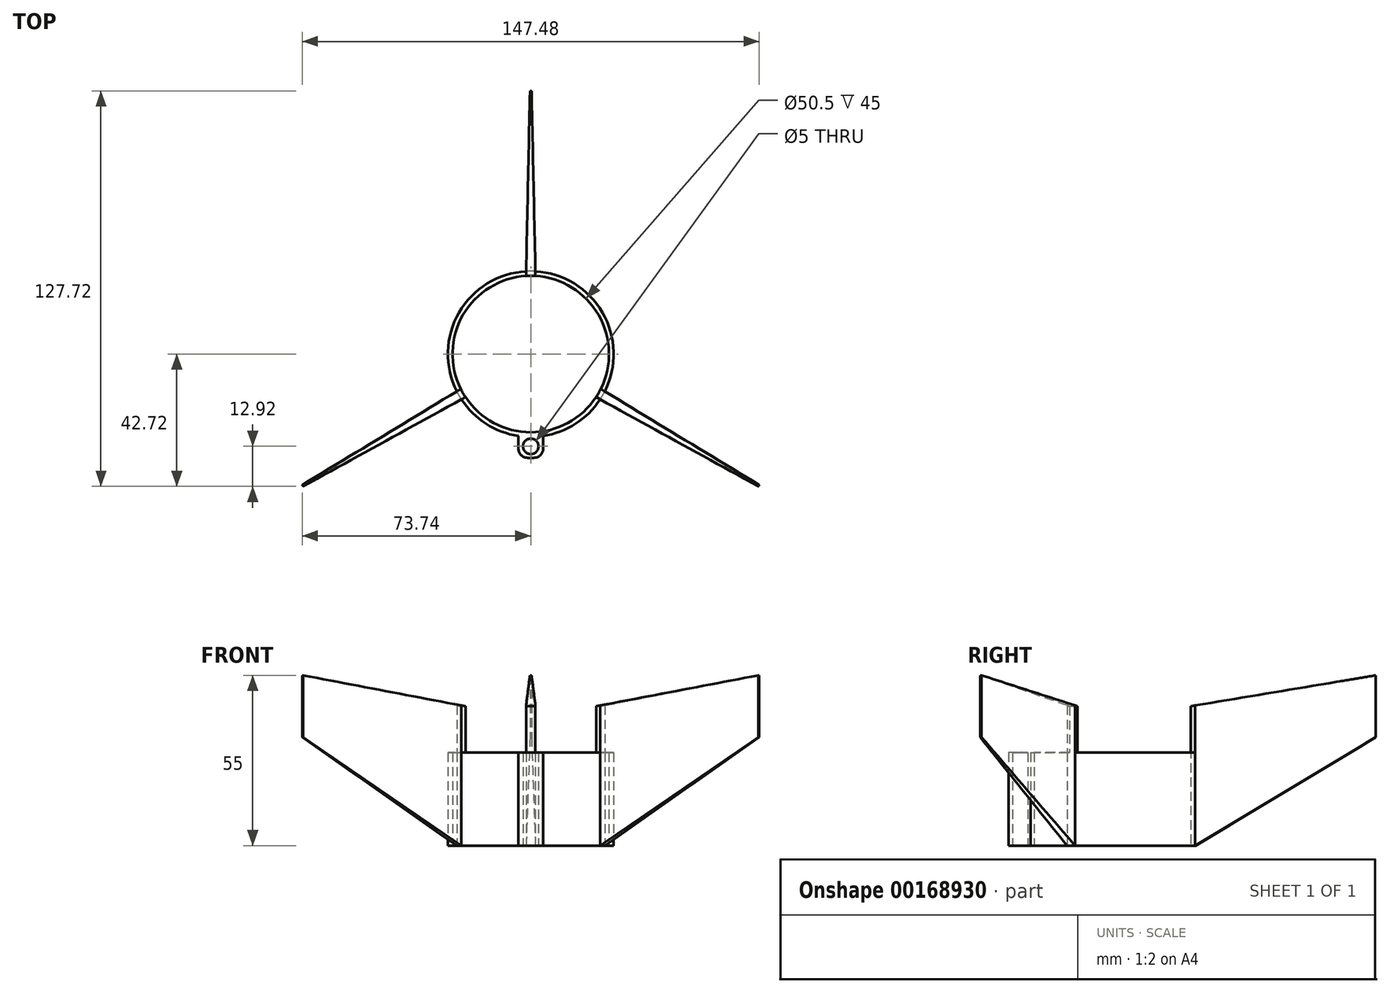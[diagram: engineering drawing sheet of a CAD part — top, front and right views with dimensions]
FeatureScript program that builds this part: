
annotation { "Feature Type Name" : "Feature", "Feature Type Description" : "" }
export const myFeature = defineFeature(function(context is Context, id is Id, definition is map)
    precondition{}
    {
        {
            var Q0;
            Q0=qCreatedBy(makeId("Top.planeOp"),FACE);
            var sketch = newSketch(context, id + "F0", { "sketchPlane" : qUnion([Q0])});
            skCircle(sketch, "E0", {"center": v(0, 0) * mm, "radius": 25.25 * mm});
            skArc(sketch, "E1", {"start": v(-22.38, -14.65) * mm, "mid": v(0, -26.75) * mm, "end": v(22.38, -14.65) * mm});
            skLineSegment(sketch, "E2", {"start": v(0, 0) * mm, "end": v(0, 85) * mm, "construction": true});
            skLineSegment(sketch, "E3", {"start": v(0, 0) * mm, "end": v(73.61, -42.5) * mm, "construction": true});
            skLineSegment(sketch, "E4", {"start": v(0, 0) * mm, "end": v(-73.61, -42.5) * mm, "construction": true});
            skLineSegment(sketch, "E5", {"start": v(0, 85) * mm, "end": v(1.5, 85) * mm});
            skLineSegment(sketch, "E6", {"start": v(0, 85) * mm, "end": v(-1.5, 85) * mm});
            skLineSegment(sketch, "E7", {"start": v(73.61, -42.5) * mm, "end": v(74.36, -41.2) * mm});
            skLineSegment(sketch, "E8", {"start": v(73.61, -42.5) * mm, "end": v(72.86, -43.8) * mm});
            skLineSegment(sketch, "E9", {"start": v(-73.61, -42.5) * mm, "end": v(-74.36, -41.2) * mm});
            skLineSegment(sketch, "E10", {"start": v(-73.61, -42.5) * mm, "end": v(-72.86, -43.8) * mm});
            skLineSegment(sketch, "E11", {"start": v(-1.5, 85) * mm, "end": v(-1.5, 26.7) * mm});
            skLineSegment(sketch, "E12", {"start": v(1.5, 85) * mm, "end": v(1.5, 26.7) * mm});
            skLineSegment(sketch, "E13", {"start": v(74.36, -41.2) * mm, "end": v(23.88, -12.05) * mm});
            skLineSegment(sketch, "E14", {"start": v(72.86, -43.8) * mm, "end": v(22.38, -14.65) * mm});
            skLineSegment(sketch, "E15", {"start": v(-72.86, -43.8) * mm, "end": v(-22.38, -14.65) * mm});
            skLineSegment(sketch, "E16", {"start": v(-74.36, -41.2) * mm, "end": v(-23.88, -12.05) * mm});
            skArc(sketch, "E17.trimOffspring", {"start": v(23.88, -12.05) * mm, "mid": v(23.17, 13.38) * mm, "end": v(1.5, 26.7) * mm});
            skArc(sketch, "E18.trimOffspring", {"start": v(-1.5, 26.7) * mm, "mid": v(-23.17, 13.37) * mm, "end": v(-23.88, -12.05) * mm});
            skSolve(sketch);
        }
        {
            var Q0;
            Q0=makeQuery(id+"F0.imprint","IMPRINT",FACE,{"disambiguationData":[TD([[makeQuery(id+"F0.imprint","IMPRINT",EDGE,{"derivedFrom":sQuery(id+"F0.wireOp",EDGE,"E0")}),-1.0]])]});
            extrude(context, id + "F1", {"entities" : qUnion([Q0]), "depth" : 30 * mm});
        }
        {
            var Q0;
            Q0=makeQuery(id+"F1.opExtrude","CAP_FACE",FACE,{"disambiguationData":[OSD([sQuery(id+"F0.wireOp",EDGE,"E0"),sQuery(id+"F0.wireOp",EDGE,"E1"),sQuery(id+"F0.wireOp",EDGE,"E5"),sQuery(id+"F0.wireOp",EDGE,"E6"),sQuery(id+"F0.wireOp",EDGE,"E7"),sQuery(id+"F0.wireOp",EDGE,"E8"),sQuery(id+"F0.wireOp",EDGE,"E9"),sQuery(id+"F0.wireOp",EDGE,"E10"),sQuery(id+"F0.wireOp",EDGE,"E11"),sQuery(id+"F0.wireOp",EDGE,"E12"),sQuery(id+"F0.wireOp",EDGE,"E13"),sQuery(id+"F0.wireOp",EDGE,"E14"),sQuery(id+"F0.wireOp",EDGE,"E15"),sQuery(id+"F0.wireOp",EDGE,"E16"),sQuery(id+"F0.wireOp",EDGE,"E17.trimOffspring"),sQuery(id+"F0.wireOp",EDGE,"E18.trimOffspring")])],"isStart":false});
            var sketch = newSketch(context, id + "F2", { "sketchPlane" : qUnion([Q0])});
            skLineSegment(sketch, "E19", {"start": v(-1.5, 85) * mm, "end": v(1.5, 85) * mm});
            skLineSegment(sketch, "E20", {"start": v(-1.5, 85) * mm, "end": v(-1.5, 25.2) * mm});
            skLineSegment(sketch, "E21", {"start": v(1.5, 85) * mm, "end": v(1.5, 25.2) * mm});
            skLineSegment(sketch, "E22", {"start": v(72.86, -43.8) * mm, "end": v(74.36, -41.2) * mm});
            skLineSegment(sketch, "E23", {"start": v(74.36, -41.2) * mm, "end": v(22.58, -11.3) * mm});
            skLineSegment(sketch, "E24", {"start": v(72.86, -43.8) * mm, "end": v(21.08, -13.9) * mm});
            skLineSegment(sketch, "E25", {"start": v(-74.36, -41.2) * mm, "end": v(-72.86, -43.8) * mm});
            skLineSegment(sketch, "E26", {"start": v(-72.86, -43.8) * mm, "end": v(-21.08, -13.9) * mm});
            skLineSegment(sketch, "E27", {"start": v(-74.36, -41.2) * mm, "end": v(-22.58, -11.3) * mm});
            skArc(sketch, "E28", {"start": v(1.5, 25.2) * mm, "mid": v(0, 25.25) * mm, "end": v(-1.5, 25.2) * mm});
            skArc(sketch, "E29.trimOffspring", {"start": v(-22.58, -11.3) * mm, "mid": v(-21.87, -12.63) * mm, "end": v(-21.08, -13.9) * mm});
            skArc(sketch, "E30.trimOffspring", {"start": v(21.08, -13.9) * mm, "mid": v(21.87, -12.63) * mm, "end": v(22.58, -11.3) * mm});
            skSolve(sketch);
        }
        {
            var Q0;
            Q0 = qSketchRegion(id + "F2", true);
            extrude(context, id + "F3", {"entities" : qUnion([Q0]), "operationType" : NewBodyOperationType.ADD, "depth" : 25 * mm});
        }
        {
            var Q0;
            Q0=makeQuery(id+"F3.boolean.opBoolean","MERGE",FACE,{"derivedFrom":[makeQuery(id+"F1.opExtrude","SWEPT_FACE",FACE,{"disambiguationData":[OSD([sQuery(id+"F0.wireOp",EDGE,"E14")])]}),makeQuery(id+"F3.opExtrude","SWEPT_FACE",FACE,{"disambiguationData":[OSD([sQuery(id+"F2.wireOp",EDGE,"E24")])]})]});
            var sketch = newSketch(context, id + "F4", { "sketchPlane" : qUnion([Q0])});
            skLineSegment(sketch, "E31", {"start": v(85, 55) * mm, "end": v(85, 35) * mm, "construction": true});
            skLineSegment(sketch, "E32", {"start": v(85, 35) * mm, "end": v(26.7, 0) * mm});
            skLineSegment(sketch, "E33", {"start": v(26.7, 0) * mm, "end": v(85, 0) * mm});
            skLineSegment(sketch, "E34", {"start": v(85, 0) * mm, "end": v(85, 35) * mm});
            skLineSegment(sketch, "E35", {"start": v(25.2, 55) * mm, "end": v(25.2, 45) * mm});
            skLineSegment(sketch, "E36", {"start": v(25.2, 45) * mm, "end": v(85, 55) * mm});
            skLineSegment(sketch, "E37", {"start": v(25.2, 55) * mm, "end": v(85, 55) * mm});
            skSolve(sketch);
        }
        {
            var Q0;
            Q0=qCreatedBy(makeId("Front.planeOp"),FACE);
            var sketch = newSketch(context, id + "F5", { "sketchPlane" : qUnion([Q0])});
            skLineSegment(sketch, "E38", {"start": v(0, 75.24) * mm, "end": v(0, -56.57) * mm, "construction": true});
            skSolve(sketch);
        }
        {
            var Q0;
            Q0 = qSketchRegion(id + "F4", true);
            var Q1;
            Q1=sQuery(id+"F5.wireOp",EDGE,"E38");
            revolve(context, id + "F6", {"operationType" : NewBodyOperationType.REMOVE, "entities" : qUnion([Q0]), "axis" : qUnion([Q1]), "revolveType" : RevolveType.FULL});
        }
        {
            var Q0;
            Q0=makeQuery(id+"F1.opExtrude","CAP_FACE",FACE,{"disambiguationData":[OSD([sQuery(id+"F0.wireOp",EDGE,"E0"),sQuery(id+"F0.wireOp",EDGE,"E1"),sQuery(id+"F0.wireOp",EDGE,"E5"),sQuery(id+"F0.wireOp",EDGE,"E6"),sQuery(id+"F0.wireOp",EDGE,"E7"),sQuery(id+"F0.wireOp",EDGE,"E8"),sQuery(id+"F0.wireOp",EDGE,"E9"),sQuery(id+"F0.wireOp",EDGE,"E10"),sQuery(id+"F0.wireOp",EDGE,"E11"),sQuery(id+"F0.wireOp",EDGE,"E12"),sQuery(id+"F0.wireOp",EDGE,"E13"),sQuery(id+"F0.wireOp",EDGE,"E14"),sQuery(id+"F0.wireOp",EDGE,"E15"),sQuery(id+"F0.wireOp",EDGE,"E16"),sQuery(id+"F0.wireOp",EDGE,"E17.trimOffspring"),sQuery(id+"F0.wireOp",EDGE,"E18.trimOffspring")])],"isStart":true});
            var sketch = newSketch(context, id + "F7", { "sketchPlane" : qUnion([Q0])});
            skLineSegment(sketch, "E39", {"start": v(-22.38, 14.65) * mm, "end": v(-23.88, 12.05) * mm, "construction": true});
            skLineSegment(sketch, "E40", {"start": v(-23.88, 12.05) * mm, "end": v(-74.54, 41.3) * mm});
            skLineSegment(sketch, "E41", {"start": v(-74.54, 41.3) * mm, "end": v(-73.92, 42.39) * mm});
            skLineSegment(sketch, "E42", {"start": v(-73.92, 42.39) * mm, "end": v(-73.67, 42.82) * mm, "construction": true});
            skLineSegment(sketch, "E43", {"start": v(-73.67, 42.82) * mm, "end": v(-73.04, 43.9) * mm});
            skLineSegment(sketch, "E44", {"start": v(-73.67, 42.82) * mm, "end": v(-22.38, 14.65) * mm});
            skLineSegment(sketch, "E45", {"start": v(-22.38, 14.65) * mm, "end": v(-73.04, 43.9) * mm});
            skLineSegment(sketch, "E46", {"start": v(-73.92, 42.39) * mm, "end": v(-23.88, 12.05) * mm});
            skLineSegment(sketch, "E47.1.0", {"start": v(0.25, -85.2) * mm, "end": v(1.5, -26.7) * mm});
            skLineSegment(sketch, "E47.1.1", {"start": v(1.5, -26.7) * mm, "end": v(1.5, -85.2) * mm});
            skLineSegment(sketch, "E47.1.2", {"start": v(1.5, -85.2) * mm, "end": v(0.25, -85.2) * mm});
            skLineSegment(sketch, "E47.1.3", {"start": v(-0.25, -85.2) * mm, "end": v(-1.5, -85.2) * mm});
            skLineSegment(sketch, "E47.1.4", {"start": v(-1.5, -26.7) * mm, "end": v(-1.5, -85.2) * mm});
            skLineSegment(sketch, "E47.1.5", {"start": v(-0.25, -85.2) * mm, "end": v(-1.5, -26.7) * mm});
            skLineSegment(sketch, "E47.2.0", {"start": v(73.67, 42.82) * mm, "end": v(22.38, 14.65) * mm});
            skLineSegment(sketch, "E47.2.1", {"start": v(22.38, 14.65) * mm, "end": v(73.04, 43.9) * mm});
            skLineSegment(sketch, "E47.2.2", {"start": v(73.04, 43.9) * mm, "end": v(73.67, 42.82) * mm});
            skLineSegment(sketch, "E47.2.3", {"start": v(73.92, 42.39) * mm, "end": v(74.54, 41.3) * mm});
            skLineSegment(sketch, "E47.2.4", {"start": v(23.88, 12.05) * mm, "end": v(74.54, 41.3) * mm});
            skLineSegment(sketch, "E47.2.5", {"start": v(73.92, 42.39) * mm, "end": v(23.88, 12.05) * mm});
            skPoint(sketch, "E47.center", {"position": v(0, 0) * mm});
            skSolve(sketch);
        }
        {
            var Q0;
            Q0 = qSketchRegion(id + "F7", true);
            extrude(context, id + "F8", {"entities" : qUnion([Q0]), "operationType" : NewBodyOperationType.REMOVE, "endBound" : BoundingType.THROUGH_ALL, "oppositeDirection" : true, "depth" : 25 * mm});
        }
        {
            var Q0;
            Q0=qCreatedBy(makeId("Top.planeOp"),FACE);
            var sketch = newSketch(context, id + "F9", { "sketchPlane" : qUnion([Q0])});
            skLineSegment(sketch, "E48", {"start": v(0, 0) * mm, "end": v(0, -67.3) * mm, "construction": true});
            skLineSegment(sketch, "E49", {"start": v(0, -33.5) * mm, "end": v(1, -33.5) * mm});
            skLineSegment(sketch, "E50", {"start": v(4, -30.5) * mm, "end": v(4, -26.39) * mm});
            skLineSegment(sketch, "E51", {"start": v(0, -33.5) * mm, "end": v(-1, -33.5) * mm});
            skLineSegment(sketch, "E52", {"start": v(-4, -30.5) * mm, "end": v(-4, -26.39) * mm});
            skLineSegment(sketch, "E53", {"start": v(-4, -26.39) * mm, "end": v(4, -26.39) * mm});
            skCircle(sketch, "E54", {"center": v(0, -29.8) * mm, "radius": 2.5 * mm});
            skPoint(sketch, "E55.visualSharp", {"position": v(-4, -33.5) * mm});
            skArc(sketch, "E55.filletArc", {"start": v(-4, -30.5) * mm, "mid": v(-3.12, -32.62) * mm, "end": v(-1, -33.5) * mm});
            skPoint(sketch, "E56.visualSharp", {"position": v(4, -33.5) * mm});
            skArc(sketch, "E56.filletArc", {"start": v(1, -33.5) * mm, "mid": v(3.12, -32.62) * mm, "end": v(4, -30.5) * mm});
            skSolve(sketch);
        }
        {
            var Q0;
            Q0 = qSketchRegion(id + "F9", true);
            extrude(context, id + "F10", {"entities" : qUnion([Q0]), "operationType" : NewBodyOperationType.ADD, "depth" : 30 * mm});
        }
    });
